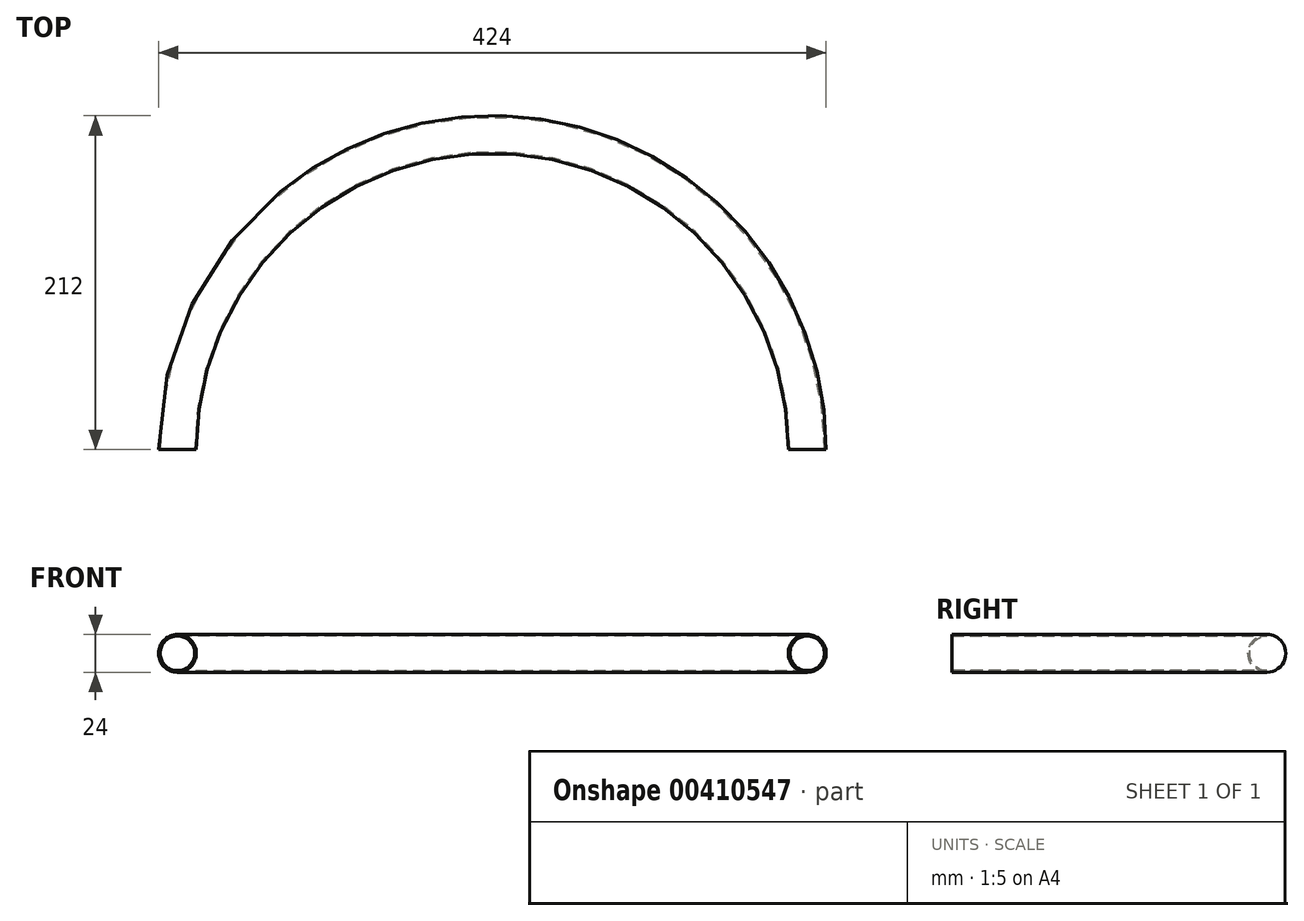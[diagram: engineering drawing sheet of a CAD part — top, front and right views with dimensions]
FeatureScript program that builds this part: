
annotation { "Feature Type Name" : "Feature", "Feature Type Description" : "" }
export const myFeature = defineFeature(function(context is Context, id is Id, definition is map)
    precondition{}
    {
        {
            var Q0;
            Q0=qCreatedBy(makeId("Top.planeOp"),FACE);
            var sketch = newSketch(context, id + "F0", { "sketchPlane" : qUnion([Q0])});
            skArc(sketch, "E0", {"start": v(200, 0) * mm, "mid": v(0, 200) * mm, "end": v(-200, 0) * mm});
            skLineSegment(sketch, "E1", {"start": v(0, 0) * mm, "end": v(232.36, 0) * mm, "construction": true});
            skLineSegment(sketch, "E2", {"start": v(0, 0) * mm, "end": v(-227.07, 0) * mm, "construction": true});
            skSolve(sketch);
        }
        {
            var Q0;
            Q0=qCreatedBy(makeId("Front.planeOp"),FACE);
            var sketch = newSketch(context, id + "F1", { "sketchPlane" : qUnion([Q0])});
            skCircle(sketch, "E3", {"center": v(-200, 0) * mm, "radius": 12 * mm});
            skCircle(sketch, "E4", {"center": v(-200, 0) * mm, "radius": 11 * mm});
            skSolve(sketch);
        }
        {
            var Q0;
            Q0=makeQuery(id+"F1.imprint","IMPRINT",FACE,{"disambiguationData":[TD([[makeQuery(id+"F1.imprint","IMPRINT",EDGE,{"derivedFrom":sQuery(id+"F1.wireOp",EDGE,"E3")}),1.0]])]});
            var Q1;
            Q1=sQuery(id+"F0.wireOp",EDGE,"E0");
            sweep(context, id + "F2", {"profiles" : qUnion([Q0]), "path" : qUnion([Q1])});
        }
    });
